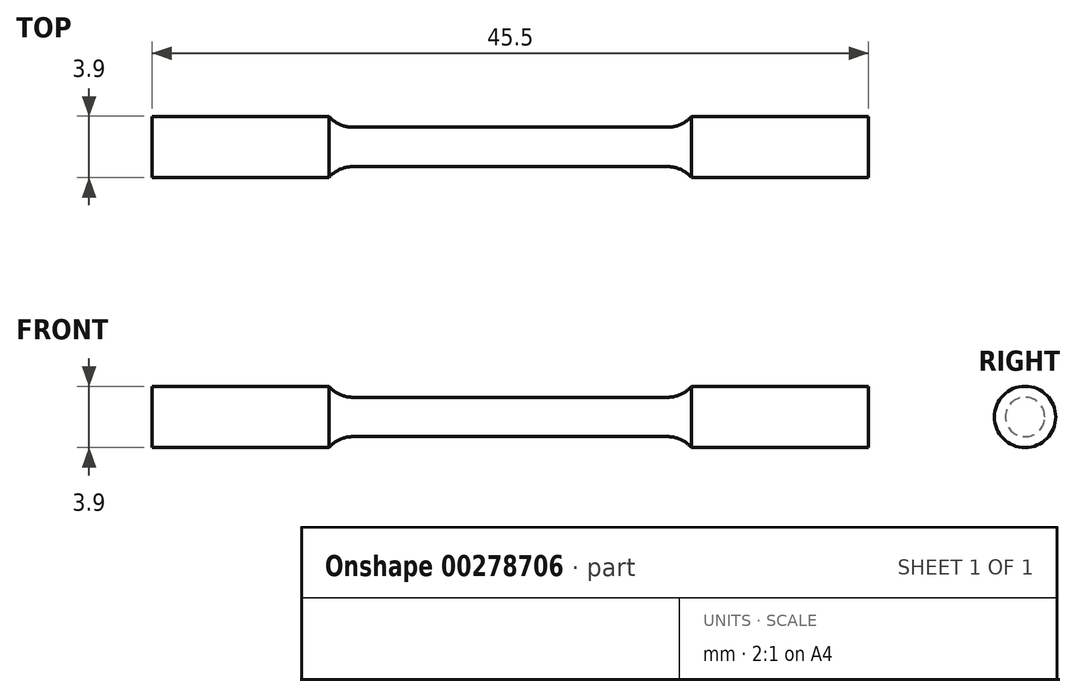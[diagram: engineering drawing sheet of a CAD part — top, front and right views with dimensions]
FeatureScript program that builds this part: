
annotation { "Feature Type Name" : "Feature", "Feature Type Description" : "" }
export const myFeature = defineFeature(function(context is Context, id is Id, definition is map)
    precondition{}
    {
        {
            var Q0;
            Q0=qCreatedBy(makeId("Front.planeOp"),FACE);
            var sketch = newSketch(context, id + "F0", { "sketchPlane" : qUnion([Q0])});
            skLineSegment(sketch, "E0", {"start": v(0, 1.25) * mm, "end": v(10, 1.25) * mm});
            skArc(sketch, "E1", {"start": v(10, 1.25) * mm, "mid": v(10.84, 1.43) * mm, "end": v(11.52, 1.95) * mm});
            skLineSegment(sketch, "E2", {"start": v(11.52, 1.95) * mm, "end": v(22.75, 1.95) * mm});
            skLineSegment(sketch, "E3", {"start": v(22.75, 1.95) * mm, "end": v(22.75, 0) * mm});
            skLineSegment(sketch, "E4.MirrorCS", {"start": v(0, 1.25) * mm, "end": v(-10, 1.25) * mm});
            skLineSegment(sketch, "E5.MirrorCS", {"start": v(-22.75, 1.95) * mm, "end": v(-22.75, 0) * mm});
            skLineSegment(sketch, "E6.MirrorCS", {"start": v(-11.52, 1.95) * mm, "end": v(-22.75, 1.95) * mm});
            skArc(sketch, "E7.MirrorCS", {"start": v(-10, 1.25) * mm, "mid": v(-10.84, 1.43) * mm, "end": v(-11.52, 1.95) * mm});
            skLineSegment(sketch, "E8", {"start": v(-22.75, 0) * mm, "end": v(22.75, 0) * mm});
            skSolve(sketch);
        }
        {
            var Q0;
            Q0 = qSketchRegion(id + "F0", true);
            var Q1;
            Q1=sQuery(id+"F0.wireOp",EDGE,"E8");
            revolve(context, id + "F1", {"entities" : qUnion([Q0]), "axis" : qUnion([Q1]), "revolveType" : RevolveType.FULL});
        }
    });
